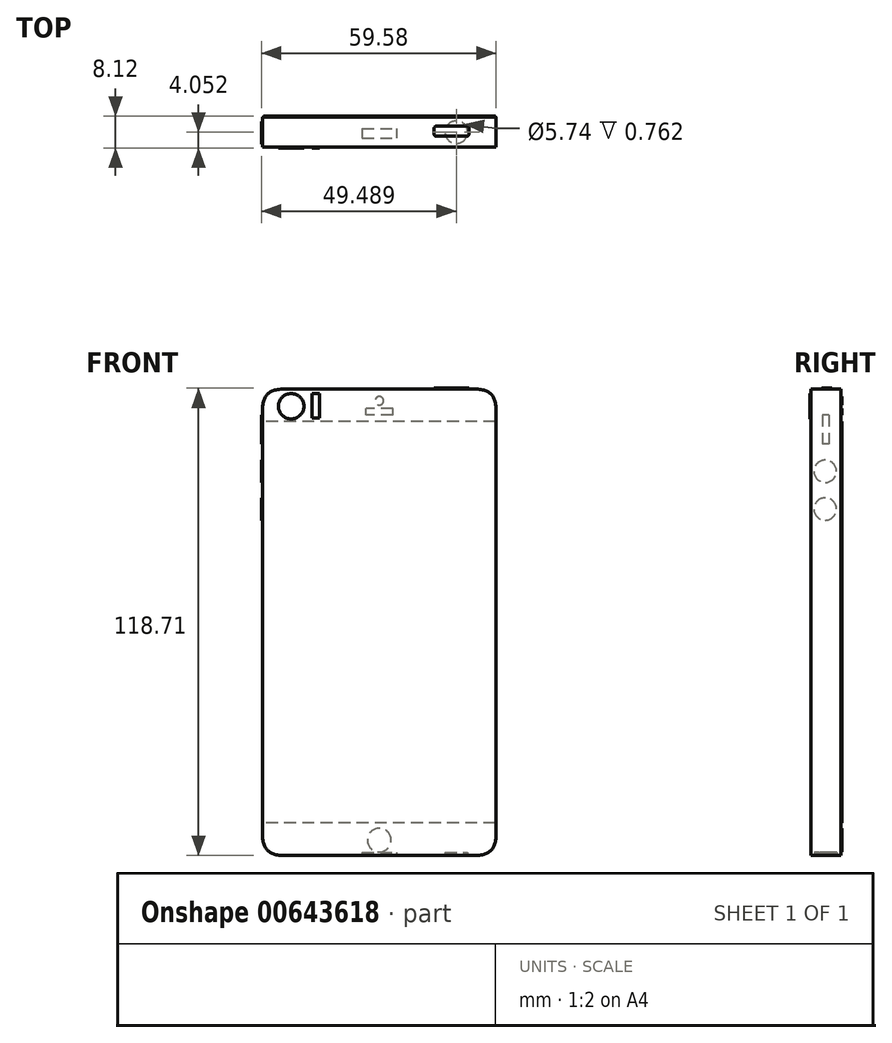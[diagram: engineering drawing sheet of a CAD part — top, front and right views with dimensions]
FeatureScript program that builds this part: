
annotation { "Feature Type Name" : "Feature", "Feature Type Description" : "" }
export const myFeature = defineFeature(function(context is Context, id is Id, definition is map)
    precondition{}
    {
        {
            var Q0;
            Q0=qCreatedBy(makeId("Front.planeOp"),FACE);
            var sketch = newSketch(context, id + "F0", { "sketchPlane" : qUnion([Q0])});
            skLineSegment(sketch, "E0.bottom", {"start": v(29.66, 59.23) * mm, "end": v(-29.66, 59.23) * mm});
            skLineSegment(sketch, "E0.top", {"start": v(29.66, -59.23) * mm, "end": v(-29.66, -59.23) * mm});
            skLineSegment(sketch, "E0.left", {"start": v(29.66, 59.23) * mm, "end": v(29.66, -59.23) * mm});
            skLineSegment(sketch, "E0.right", {"start": v(-29.66, 59.23) * mm, "end": v(-29.66, -59.23) * mm});
            skPoint(sketch, "E0.middle", {"position": v(0, 0) * mm});
            skSolve(sketch);
        }
        {
            var Q0;
            Q0=makeQuery(id+"F0.imprint","IMPRINT",FACE,{"disambiguationData":[TD([[makeQuery(id+"F0.imprint","IMPRINT",EDGE,{"derivedFrom":sQuery(id+"F0.wireOp",EDGE,"E0.bottom")}),1.0]])]});
            extrude(context, id + "F1", {"entities" : qUnion([Q0]), "depth" : 7.62 * mm, "offsetDistance" : 25.4 * mm});
        }
        {
            var Q0;
            Q0=makeQuery(id+"F1.opExtrude","SWEPT_EDGE",EDGE,{"disambiguationData":[OSD([sQuery(id+"F0.wireOp",EDGE,"E0.bottom"),sQuery(id+"F0.wireOp",EDGE,"E0.left")])]});
            fillet(context, id + "F2", {"entities" : qUnion([Q0]), "radius" : 5.08 * mm, "tangentPropagation" : true, "rho" : 0.5, "crossSection" : FilletCrossSection.CONIC, "allowEdgeOverflow" : false});
        }
        {
            var Q0;
            Q0=makeQuery(id+"F1.opExtrude","SWEPT_EDGE",EDGE,{"disambiguationData":[OSD([sQuery(id+"F0.wireOp",EDGE,"E0.bottom"),sQuery(id+"F0.wireOp",EDGE,"E0.right")])]});
            fillet(context, id + "F3", {"entities" : qUnion([Q0]), "radius" : 5.08 * mm, "tangentPropagation" : true, "rho" : 0.5, "crossSection" : FilletCrossSection.CONIC, "allowEdgeOverflow" : false});
        }
        {
            var Q0;
            Q0=makeQuery(id+"F1.opExtrude","SWEPT_EDGE",EDGE,{"disambiguationData":[OSD([sQuery(id+"F0.wireOp",EDGE,"E0.top"),sQuery(id+"F0.wireOp",EDGE,"E0.right")])]});
            fillet(context, id + "F4", {"entities" : qUnion([Q0]), "radius" : 5.08 * mm, "tangentPropagation" : true, "rho" : 0.5, "crossSection" : FilletCrossSection.CONIC, "allowEdgeOverflow" : false});
        }
        {
            var Q0;
            Q0=makeQuery(id+"F1.opExtrude","SWEPT_EDGE",EDGE,{"disambiguationData":[OSD([sQuery(id+"F0.wireOp",EDGE,"E0.top"),sQuery(id+"F0.wireOp",EDGE,"E0.left")])]});
            fillet(context, id + "F5", {"entities" : qUnion([Q0]), "radius" : 5.08 * mm, "tangentPropagation" : true, "rho" : 0.5, "crossSection" : FilletCrossSection.CONIC, "allowEdgeOverflow" : false});
        }
        {
            var Q0;
            Q0=qCreatedBy(makeId("Front.planeOp"),FACE);
            var sketch = newSketch(context, id + "F6", { "sketchPlane" : qUnion([Q0])});
            skLineSegment(sketch, "E1.bottom", {"start": v(29.46, -50.97) * mm, "end": v(-29.46, -50.97) * mm});
            skLineSegment(sketch, "E1.top", {"start": v(29.46, 50.97) * mm, "end": v(-29.46, 50.97) * mm});
            skLineSegment(sketch, "E1.left", {"start": v(29.46, -50.97) * mm, "end": v(29.46, 50.97) * mm});
            skLineSegment(sketch, "E1.right", {"start": v(-29.46, -50.97) * mm, "end": v(-29.46, 50.97) * mm});
            skPoint(sketch, "E1.middle", {"position": v(0, 0) * mm});
            skSolve(sketch);
        }
        {
            var Q0;
            Q0=makeQuery(id+"F1.opExtrude","CAP_FACE",FACE,{"disambiguationData":[OSD([sQuery(id+"F0.wireOp",EDGE,"E0.bottom"),sQuery(id+"F0.wireOp",EDGE,"E0.top"),sQuery(id+"F0.wireOp",EDGE,"E0.left"),sQuery(id+"F0.wireOp",EDGE,"E0.right")])],"isStart":true});
            var sketch = newSketch(context, id + "F7", { "sketchPlane" : qUnion([Q0])});
            skCircle(sketch, "E2", {"center": v(0, 56.27) * mm, "radius": 1.08 * mm});
            skSolve(sketch);
        }
        {
            var Q0;
            Q0=qCreatedBy(makeId("Front.planeOp"),FACE);
            var sketch = newSketch(context, id + "F8", { "sketchPlane" : qUnion([Q0])});
            skCircle(sketch, "E3", {"center": v(0, -55.36) * mm, "radius": 3.01 * mm});
            skSolve(sketch);
        }
        {
            var Q0;
            Q0=makeQuery(id+"F7.imprint","IMPRINT",FACE,{"disambiguationData":[TD([[makeQuery(id+"F7.imprint","IMPRINT",EDGE,{"derivedFrom":sQuery(id+"F7.wireOp",EDGE,"E2")}),-1.0]])]});
            var sketch = newSketch(context, id + "F9", { "sketchPlane" : qUnion([Q0])});
            skLineSegment(sketch, "E4.bottom", {"start": v(-3.43, 52.6) * mm, "end": v(3.43, 52.6) * mm});
            skLineSegment(sketch, "E4.top", {"start": v(-3.43, 54.25) * mm, "end": v(3.43, 54.25) * mm});
            skLineSegment(sketch, "E4.left", {"start": v(-3.43, 52.6) * mm, "end": v(-3.43, 54.25) * mm});
            skLineSegment(sketch, "E4.right", {"start": v(3.43, 52.6) * mm, "end": v(3.43, 54.25) * mm});
            skPoint(sketch, "E4.middle", {"position": v(0, 53.43) * mm});
            skSolve(sketch);
        }
        {
            var Q0;
            Q0=makeQuery(id+"F1.opExtrude","SWEPT_FACE",FACE,{"disambiguationData":[OSD([sQuery(id+"F0.wireOp",EDGE,"E0.right")])]});
            var sketch = newSketch(context, id + "F10", { "sketchPlane" : qUnion([Q0])});
            skCircle(sketch, "E5", {"center": v(3.97, 38.36) * mm, "radius": 2.86 * mm});
            skSolve(sketch);
        }
        {
            var Q0;
            Q0=makeQuery(id+"F10.imprint","IMPRINT",FACE,{"disambiguationData":[TD([[makeQuery(id+"F10.imprint","IMPRINT",EDGE,{"derivedFrom":sQuery(id+"F10.wireOp",EDGE,"E5")}),-1.0]])]});
            var sketch = newSketch(context, id + "F11", { "sketchPlane" : qUnion([Q0])});
            skCircle(sketch, "E6", {"center": v(3.97, 28.77) * mm, "radius": 2.86 * mm});
            skSolve(sketch);
        }
        {
            var Q0;
            Q0=makeQuery(id+"F10.imprint","IMPRINT",FACE,{"disambiguationData":[TD([[makeQuery(id+"F10.imprint","IMPRINT",EDGE,{"derivedFrom":sQuery(id+"F10.wireOp",EDGE,"E5")}),-1.0]])]});
            var sketch = newSketch(context, id + "F12", { "sketchPlane" : qUnion([Q0])});
            skLineSegment(sketch, "E7.bottom", {"start": v(3.06, 52.7) * mm, "end": v(4.68, 52.7) * mm});
            skLineSegment(sketch, "E7.top", {"start": v(3.06, 45.32) * mm, "end": v(4.68, 45.32) * mm});
            skLineSegment(sketch, "E7.left", {"start": v(3.06, 52.7) * mm, "end": v(3.06, 45.32) * mm});
            skLineSegment(sketch, "E7.right", {"start": v(4.68, 52.7) * mm, "end": v(4.68, 45.32) * mm});
            skSolve(sketch);
        }
        {
            var Q0;
            Q0=makeQuery(id+"F1.opExtrude","CAP_FACE",FACE,{"disambiguationData":[OSD([sQuery(id+"F0.wireOp",EDGE,"E0.bottom"),sQuery(id+"F0.wireOp",EDGE,"E0.top"),sQuery(id+"F0.wireOp",EDGE,"E0.left"),sQuery(id+"F0.wireOp",EDGE,"E0.right")])],"isStart":false});
            var sketch = newSketch(context, id + "F13", { "sketchPlane" : qUnion([Q0])});
            skCircle(sketch, "E8", {"center": v(-22.39, 54.89) * mm, "radius": 3.23 * mm});
            skSolve(sketch);
        }
        {
            var Q0;
            Q0=makeQuery(id+"F13.imprint","IMPRINT",FACE,{"disambiguationData":[TD([[makeQuery(id+"F13.imprint","IMPRINT",EDGE,{"derivedFrom":sQuery(id+"F13.wireOp",EDGE,"E8")}),-1.0]])]});
            var sketch = newSketch(context, id + "F14", { "sketchPlane" : qUnion([Q0])});
            skLineSegment(sketch, "E9.bottom", {"start": v(-17.13, 58.08) * mm, "end": v(-15.23, 58.08) * mm});
            skLineSegment(sketch, "E9.top", {"start": v(-17.13, 51.92) * mm, "end": v(-15.23, 51.92) * mm});
            skLineSegment(sketch, "E9.left", {"start": v(-17.13, 58.08) * mm, "end": v(-17.13, 51.92) * mm});
            skLineSegment(sketch, "E9.right", {"start": v(-15.23, 58.08) * mm, "end": v(-15.23, 51.92) * mm});
            skSolve(sketch);
        }
        {
            var Q0;
            Q0=makeQuery(id+"F1.opExtrude","SWEPT_FACE",FACE,{"disambiguationData":[OSD([sQuery(id+"F0.wireOp",EDGE,"E0.top")])]});
            var sketch = newSketch(context, id + "F15", { "sketchPlane" : qUnion([Q0])});
            skCircle(sketch, "E10", {"center": v(19.57, 3.82) * mm, "radius": 2.87 * mm});
            skSolve(sketch);
        }
        {
            var Q0;
            Q0=makeQuery(id+"F15.imprint","IMPRINT",FACE,{"disambiguationData":[TD([[makeQuery(id+"F15.imprint","IMPRINT",EDGE,{"derivedFrom":sQuery(id+"F15.wireOp",EDGE,"E10")}),-1.0]])]});
            var sketch = newSketch(context, id + "F16", { "sketchPlane" : qUnion([Q0])});
            skLineSegment(sketch, "E11.bottom", {"start": v(-4.33, 2.86) * mm, "end": v(4.33, 2.86) * mm});
            skLineSegment(sketch, "E11.top", {"start": v(-4.33, 5.33) * mm, "end": v(4.33, 5.33) * mm});
            skLineSegment(sketch, "E11.left", {"start": v(-4.33, 2.86) * mm, "end": v(-4.33, 5.33) * mm});
            skLineSegment(sketch, "E11.right", {"start": v(4.33, 2.86) * mm, "end": v(4.33, 5.33) * mm});
            skPoint(sketch, "E11.middle", {"position": v(0, 4.1) * mm});
            skSolve(sketch);
        }
        {
            var Q0;
            Q0=makeQuery(id+"F1.opExtrude","SWEPT_FACE",FACE,{"disambiguationData":[OSD([sQuery(id+"F0.wireOp",EDGE,"E0.bottom")])]});
            var sketch = newSketch(context, id + "F17", { "sketchPlane" : qUnion([Q0])});
            skLineSegment(sketch, "E12.bottom", {"start": v(13.95, -4.83) * mm, "end": v(22.76, -4.83) * mm});
            skLineSegment(sketch, "E12.top", {"start": v(13.95, -2.31) * mm, "end": v(22.76, -2.31) * mm});
            skLineSegment(sketch, "E12.left", {"start": v(13.95, -4.83) * mm, "end": v(13.95, -2.31) * mm});
            skLineSegment(sketch, "E12.right", {"start": v(22.76, -4.83) * mm, "end": v(22.76, -2.31) * mm});
            skPoint(sketch, "E12.middle", {"position": v(18.35, -3.57) * mm});
            skSolve(sketch);
        }
        {
            var Q0;
            Q0 = qSketchRegion(id + "F17", true);
            extrude(context, id + "F18", {"entities" : qUnion([Q0]), "operationType" : NewBodyOperationType.ADD, "depth" : 0.25 * mm, "offsetDistance" : 25.4 * mm});
        }
        {
            var Q0;
            Q0=makeQuery(id+"F18.opExtrude","SWEPT_EDGE",EDGE,{"disambiguationData":[OSD([sQuery(id+"F17.wireOp",EDGE,"E12.top"),sQuery(id+"F17.wireOp",EDGE,"E12.right")])]});
            fillet(context, id + "F19", {"entities" : qUnion([Q0]), "radius" : 0.5 * mm, "tangentPropagation" : true, "rho" : 0.5, "crossSection" : FilletCrossSection.CONIC, "allowEdgeOverflow" : false});
        }
        {
            var Q0;
            Q0=makeQuery(id+"F18.opExtrude","SWEPT_EDGE",EDGE,{"disambiguationData":[OSD([sQuery(id+"F17.wireOp",EDGE,"E12.top"),sQuery(id+"F17.wireOp",EDGE,"E12.left")])]});
            var Q1;
            Q1=makeQuery(id+"F18.opExtrude","SWEPT_EDGE",EDGE,{"disambiguationData":[OSD([sQuery(id+"F17.wireOp",EDGE,"E12.bottom"),sQuery(id+"F17.wireOp",EDGE,"E12.right")])]});
            var Q2;
            Q2=makeQuery(id+"F18.opExtrude","SWEPT_EDGE",EDGE,{"disambiguationData":[OSD([sQuery(id+"F17.wireOp",EDGE,"E12.bottom"),sQuery(id+"F17.wireOp",EDGE,"E12.left")])]});
            fillet(context, id + "F20", {"entities" : qUnion([Q0, Q1, Q2]), "radius" : 0.5 * mm, "tangentPropagation" : true, "allowEdgeOverflow" : false});
        }
        {
            var Q0;
            Q0 = qSketchRegion(id + "F10", true);
            extrude(context, id + "F21", {"entities" : qUnion([Q0]), "operationType" : NewBodyOperationType.ADD, "depth" : 0.25 * mm, "offsetDistance" : 25.4 * mm});
        }
        {
            var Q0;
            Q0 = qSketchRegion(id + "F11", true);
            extrude(context, id + "F22", {"entities" : qUnion([Q0]), "operationType" : NewBodyOperationType.ADD, "depth" : 0.25 * mm, "offsetDistance" : 25.4 * mm});
        }
        {
            var Q0;
            Q0 = qSketchRegion(id + "F12", true);
            extrude(context, id + "F23", {"entities" : qUnion([Q0]), "operationType" : NewBodyOperationType.ADD, "depth" : 0.25 * mm, "offsetDistance" : 25.4 * mm});
        }
        {
            var Q0;
            Q0 = qSketchRegion(id + "F7", true);
            extrude(context, id + "F24", {"entities" : qUnion([Q0]), "operationType" : NewBodyOperationType.ADD, "depth" : 0.25 * mm, "offsetDistance" : 25.4 * mm});
        }
        {
            var Q0;
            Q0 = qSketchRegion(id + "F9", true);
            extrude(context, id + "F25", {"entities" : qUnion([Q0]), "operationType" : NewBodyOperationType.ADD, "depth" : 0.25 * mm, "offsetDistance" : 25.4 * mm});
        }
        {
            var Q0;
            Q0 = qSketchRegion(id + "F13", true);
            extrude(context, id + "F26", {"entities" : qUnion([Q0]), "operationType" : NewBodyOperationType.ADD, "depth" : 0.25 * mm, "offsetDistance" : 25.4 * mm});
        }
        {
            var Q0;
            Q0 = qSketchRegion(id + "F14", true);
            extrude(context, id + "F27", {"entities" : qUnion([Q0]), "operationType" : NewBodyOperationType.ADD, "depth" : 0.25 * mm, "offsetDistance" : 25.4 * mm});
        }
        {
            var Q0;
            Q0 = qSketchRegion(id + "F8", true);
            extrude(context, id + "F28", {"entities" : qUnion([Q0]), "operationType" : NewBodyOperationType.ADD, "oppositeDirection" : true, "depth" : 0.25 * mm, "offsetDistance" : 25.4 * mm});
        }
        {
            var Q0;
            Q0 = qSketchRegion(id + "F6", true);
            extrude(context, id + "F29", {"entities" : qUnion([Q0]), "operationType" : NewBodyOperationType.ADD, "oppositeDirection" : true, "depth" : 0.25 * mm, "offsetDistance" : 25.4 * mm});
        }
        {
            var Q0;
            Q0 = qSketchRegion(id + "F16", true);
            extrude(context, id + "F30", {"entities" : qUnion([Q0]), "operationType" : NewBodyOperationType.REMOVE, "oppositeDirection" : true, "depth" : 0.76 * mm, "offsetDistance" : 25.4 * mm});
        }
        {
            var Q0;
            Q0 = qSketchRegion(id + "F15", true);
            extrude(context, id + "F31", {"entities" : qUnion([Q0]), "operationType" : NewBodyOperationType.REMOVE, "oppositeDirection" : true, "depth" : 0.76 * mm, "offsetDistance" : 25.4 * mm});
        }
    });
